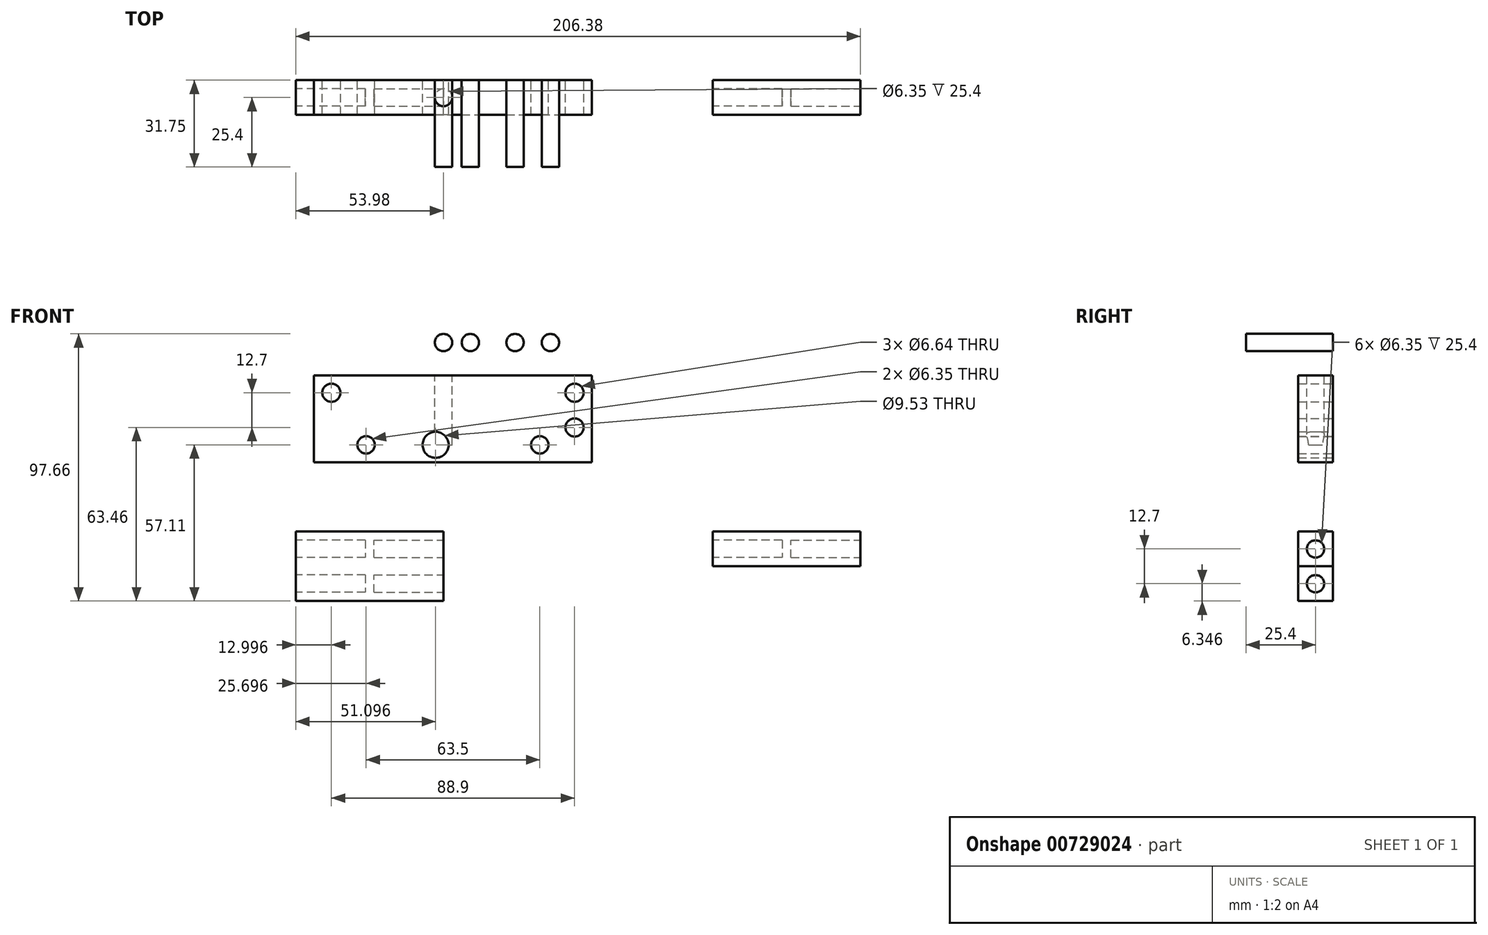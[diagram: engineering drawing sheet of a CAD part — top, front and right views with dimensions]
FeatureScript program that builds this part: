
annotation { "Feature Type Name" : "Feature", "Feature Type Description" : "" }
export const myFeature = defineFeature(function(context is Context, id is Id, definition is map)
    precondition{}
    {
        {
            var Q0;
            Q0=qCreatedBy(makeId("Front.planeOp"),FACE);
            var sketch = newSketch(context, id + "F0", { "sketchPlane" : qUnion([Q0])});
            skLineSegment(sketch, "E0.bottom", {"start": v(-47.33, 31.75) * mm, "end": v(54.27, 31.75) * mm});
            skLineSegment(sketch, "E0.top", {"start": v(-47.33, 0) * mm, "end": v(54.27, 0) * mm});
            skLineSegment(sketch, "E0.left", {"start": v(-47.33, 31.75) * mm, "end": v(-47.33, 0) * mm});
            skLineSegment(sketch, "E0.right", {"start": v(54.27, 31.75) * mm, "end": v(54.27, 0) * mm});
            skLineSegment(sketch, "E1.bottom", {"start": v(0, -50.76) * mm, "end": v(-53.98, -50.76) * mm});
            skLineSegment(sketch, "E1.top", {"start": v(0, -25.36) * mm, "end": v(-53.97, -25.36) * mm});
            skLineSegment(sketch, "E1.left", {"start": v(0, -50.76) * mm, "end": v(0, -25.36) * mm});
            skLineSegment(sketch, "E1.right", {"start": v(-53.98, -50.76) * mm, "end": v(-53.98, -25.36) * mm});
            skCircle(sketch, "E2", {"center": v(-40.98, 25.4) * mm, "radius": 3.32 * mm});
            skCircle(sketch, "E3", {"center": v(47.92, 25.4) * mm, "radius": 3.32 * mm});
            skCircle(sketch, "E4", {"center": v(47.92, 12.7) * mm, "radius": 3.32 * mm});
            skLineSegment(sketch, "E5.bottom", {"start": v(47.92, 12.7) * mm, "end": v(47.92, 12.7) * mm});
            skLineSegment(sketch, "E5.top", {"start": v(47.92, 0) * mm, "end": v(47.92, 0) * mm});
            skLineSegment(sketch, "E5.left", {"start": v(47.92, 12.7) * mm, "end": v(47.92, 0) * mm});
            skLineSegment(sketch, "E5.right", {"start": v(47.92, 12.7) * mm, "end": v(47.92, 0) * mm});
            skLineSegment(sketch, "E6", {"start": v(-2.88, 31.75) * mm, "end": v(-2.88, 0) * mm});
            skCircle(sketch, "E7", {"center": v(-2.88, 6.35) * mm, "radius": 4.76 * mm});
            skLineSegment(sketch, "E8", {"start": v(-47.33, 6.35) * mm, "end": v(54.27, 6.35) * mm});
            skCircle(sketch, "E9", {"center": v(35.22, 6.35) * mm, "radius": 3.18 * mm});
            skCircle(sketch, "E10", {"center": v(-28.28, 6.35) * mm, "radius": 3.18 * mm});
            skSolve(sketch);
        }
        {
            var Q0;
            Q0 = qSketchRegion(id + "F0", true);
            extrude(context, id + "F1", {"entities" : qUnion([Q0]), "depth" : 12.7 * mm, "offsetDistance" : 25.4 * mm});
        }
        {
            var Q0;
            Q0=makeQuery(id+"F1.opExtrude","SWEPT_FACE",FACE,{"disambiguationData":[OSD([sQuery(id+"F0.wireOp",EDGE,"E1.right")])]});
            var sketch = newSketch(context, id + "F2", { "sketchPlane" : qUnion([Q0])});
            skLineSegment(sketch, "E11", {"start": v(6.35, -25.36) * mm, "end": v(6.35, -50.76) * mm});
            skCircle(sketch, "E12", {"center": v(6.35, -31.71) * mm, "radius": 3.18 * mm});
            skCircle(sketch, "E13", {"center": v(6.35, -44.41) * mm, "radius": 3.18 * mm});
            skSolve(sketch);
        }
        {
            var Q0;
            Q0 = qSketchRegion(id + "F2", true);
            extrude(context, id + "F3", {"entities" : qUnion([Q0]), "operationType" : NewBodyOperationType.REMOVE, "oppositeDirection" : true, "depth" : 25.4 * mm, "offsetDistance" : 25.4 * mm});
        }
        {
            var Q0;
            Q0=makeQuery(id+"F1.opExtrude","SWEPT_FACE",FACE,{"disambiguationData":[OSD([sQuery(id+"F0.wireOp",EDGE,"E1.left")])]});
            var sketch = newSketch(context, id + "F4", { "sketchPlane" : qUnion([Q0])});
            skLineSegment(sketch, "E14", {"start": v(-6.35, -25.36) * mm, "end": v(-6.35, -50.76) * mm});
            skCircle(sketch, "E15", {"center": v(-6.35, -31.71) * mm, "radius": 3.18 * mm});
            skCircle(sketch, "E16", {"center": v(-6.35, -44.41) * mm, "radius": 3.18 * mm});
            skSolve(sketch);
        }
        {
            var Q0;
            Q0 = qSketchRegion(id + "F4", true);
            extrude(context, id + "F5", {"entities" : qUnion([Q0]), "operationType" : NewBodyOperationType.REMOVE, "oppositeDirection" : true, "depth" : 25.4 * mm, "offsetDistance" : 25.4 * mm});
        }
        {
            var Q0;
            Q0=qCreatedBy(makeId("Front.planeOp"),FACE);
            var sketch = newSketch(context, id + "F6", { "sketchPlane" : qUnion([Q0])});
            skCircle(sketch, "E17", {"center": v(39.08, 43.73) * mm, "radius": 3.18 * mm});
            skCircle(sketch, "E18", {"center": v(26.16, 43.73) * mm, "radius": 3.18 * mm});
            skCircle(sketch, "E19", {"center": v(0, 43.73) * mm, "radius": 3.18 * mm});
            skCircle(sketch, "E20", {"center": v(9.83, 43.73) * mm, "radius": 3.18 * mm});
            skLineSegment(sketch, "E21", {"start": v(45.45, 43.73) * mm, "end": v(-4.57, 43.73) * mm});
            skSolve(sketch);
        }
        {
            var Q0;
            Q0 = qSketchRegion(id + "F6", true);
            extrude(context, id + "F7", {"entities" : qUnion([Q0]), "depth" : 31.75 * mm, "offsetDistance" : 25.4 * mm});
        }
        {
            var Q0;
            Q0=makeQuery(id+"F1.opExtrude","SWEPT_FACE",FACE,{"disambiguationData":[OSD([sQuery(id+"F0.wireOp",EDGE,"E0.bottom")])]});
            var sketch = newSketch(context, id + "F8", { "sketchPlane" : qUnion([Q0])});
            skLineSegment(sketch, "E22", {"start": v(0, 0) * mm, "end": v(0, -12.7) * mm});
            skPoint(sketch, "E22.endSnap0", {"position": v(3.47, -12.7) * mm});
            skCircle(sketch, "E23", {"center": v(0, -6.35) * mm, "radius": 3.18 * mm});
            skPoint(sketch, "E23.perimeterSnap0", {"position": v(0, -6.35) * mm});
            skPoint(sketch, "E23.perimeterSnap1", {"position": v(3.47, 0) * mm});
            skSolve(sketch);
        }
        {
            var Q0;
            Q0 = qSketchRegion(id + "F8", true);
            extrude(context, id + "F9", {"entities" : qUnion([Q0]), "operationType" : NewBodyOperationType.REMOVE, "oppositeDirection" : true, "depth" : 25.4 * mm, "offsetDistance" : 25.4 * mm});
        }
        {
            var Q0;
            Q0=makeQuery(id+"F1.opExtrude","SWEPT_BODY",BODY,{"disambiguationData":[OSD([sQuery(id+"F0.wireOp",EDGE,"E1.bottom"),sQuery(id+"F0.wireOp",EDGE,"E1.top"),sQuery(id+"F0.wireOp",EDGE,"E1.left"),sQuery(id+"F0.wireOp",EDGE,"E1.right")])]});
            transform(context, id + "F10", {"entities" : qUnion([Q0]), "transformType" : TransformType.TRANSLATION_3D, "dx" : 152.4 * mm, "dy" : 0 * mm, "dz" : 0 * mm, "makeCopy" : true});
        }
        {
            var Q0;
            Q0=makeQuery(id+"F10.opPattern","COPY",FACE,{"derivedFrom":makeQuery(id+"F1.opExtrude","CAP_FACE",FACE,{"disambiguationData":[OSD([sQuery(id+"F0.wireOp",EDGE,"E1.bottom"),sQuery(id+"F0.wireOp",EDGE,"E1.top"),sQuery(id+"F0.wireOp",EDGE,"E1.left"),sQuery(id+"F0.wireOp",EDGE,"E1.right")])],"isStart":true}),"instanceName":"1"});
            var sketch = newSketch(context, id + "F11", { "sketchPlane" : qUnion([Q0])});
            skLineSegment(sketch, "E24", {"start": v(-152.4, -38.06) * mm, "end": v(-98.43, -38.06) * mm});
            skLineSegment(sketch, "E25", {"start": v(-98.43, -38.06) * mm, "end": v(-98.43, -50.76) * mm});
            skLineSegment(sketch, "E26", {"start": v(-98.43, -50.76) * mm, "end": v(-152.4, -50.76) * mm});
            skLineSegment(sketch, "E27", {"start": v(-152.4, -50.76) * mm, "end": v(-152.4, -38.06) * mm});
            skSolve(sketch);
        }
        {
            var Q0;
            Q0 = qSketchRegion(id + "F11", true);
            extrude(context, id + "F12", {"entities" : qUnion([Q0]), "operationType" : NewBodyOperationType.REMOVE, "oppositeDirection" : true, "depth" : 25.4 * mm, "offsetDistance" : 25.4 * mm});
        }
    });
